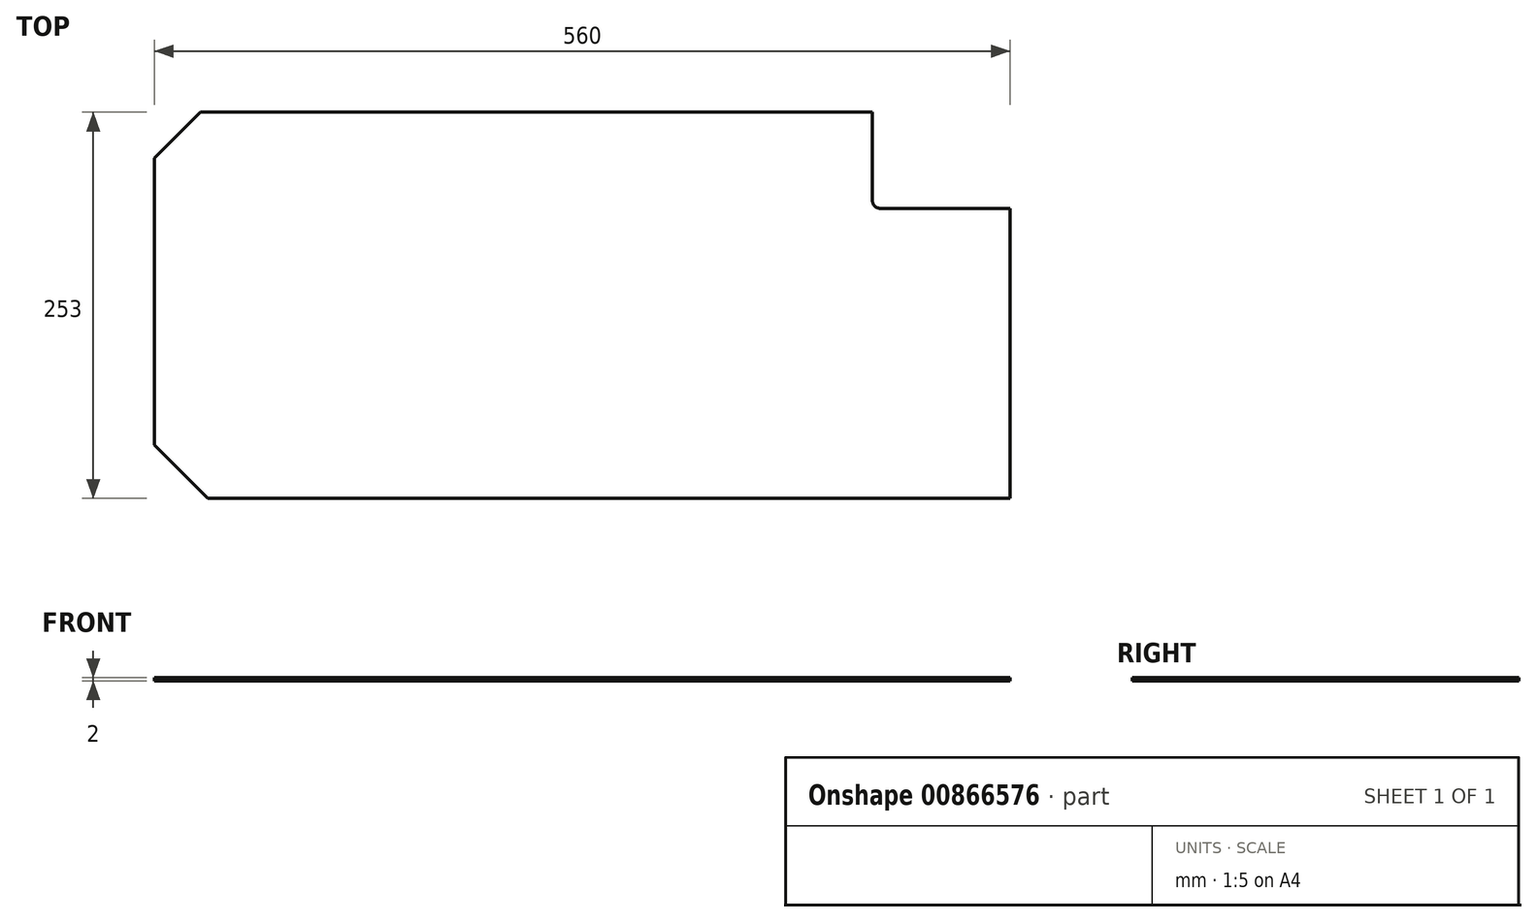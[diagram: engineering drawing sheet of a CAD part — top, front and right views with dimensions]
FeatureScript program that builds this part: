
annotation { "Feature Type Name" : "Feature", "Feature Type Description" : "" }
export const myFeature = defineFeature(function(context is Context, id is Id, definition is map)
    precondition{}
    {
        {
            var Q0;
            Q0=qCreatedBy(makeId("Top.planeOp"),FACE);
            var sketch = newSketch(context, id + "F0", { "sketchPlane" : qUnion([Q0])});
            skLineSegment(sketch, "E0", {"start": v(-22.31, 218) * mm, "end": v(417.69, 218) * mm});
            skLineSegment(sketch, "E1", {"start": v(507.69, -35) * mm, "end": v(-17.31, -35) * mm});
            skLineSegment(sketch, "E2", {"start": v(507.69, -35) * mm, "end": v(507.69, 155) * mm});
            skLineSegment(sketch, "E3", {"start": v(507.69, 155) * mm, "end": v(422.69, 155) * mm});
            skLineSegment(sketch, "E4", {"start": v(417.69, 160) * mm, "end": v(417.69, 218) * mm});
            skPoint(sketch, "E5.visualSharp", {"position": v(417.69, 155) * mm});
            skArc(sketch, "E5.filletArc", {"start": v(417.69, 160) * mm, "mid": v(419.15, 156.46) * mm, "end": v(422.69, 155) * mm});
            skLineSegment(sketch, "E6", {"start": v(-52.31, 0) * mm, "end": v(-52.31, 188) * mm});
            skLineSegment(sketch, "E7", {"start": v(-22.31, 218) * mm, "end": v(-52.31, 188) * mm});
            skPoint(sketch, "E8.orphan", {"position": v(-52.31, 218) * mm});
            skLineSegment(sketch, "E9", {"start": v(-17.31, -35) * mm, "end": v(-52.31, 0) * mm});
            skSolve(sketch);
        }
        {
            var Q0;
            Q0=makeQuery(id+"F0.imprint","IMPRINT",FACE,{"disambiguationData":[TD([[makeQuery(id+"F0.imprint","IMPRINT",EDGE,{"derivedFrom":sQuery(id+"F0.wireOp",EDGE,"E0")}),-1.0]])]});
            extrude(context, id + "F1", {"entities" : qUnion([Q0]), "depth" : 2 * mm, "offsetDistance" : 25 * mm});
        }
    });
